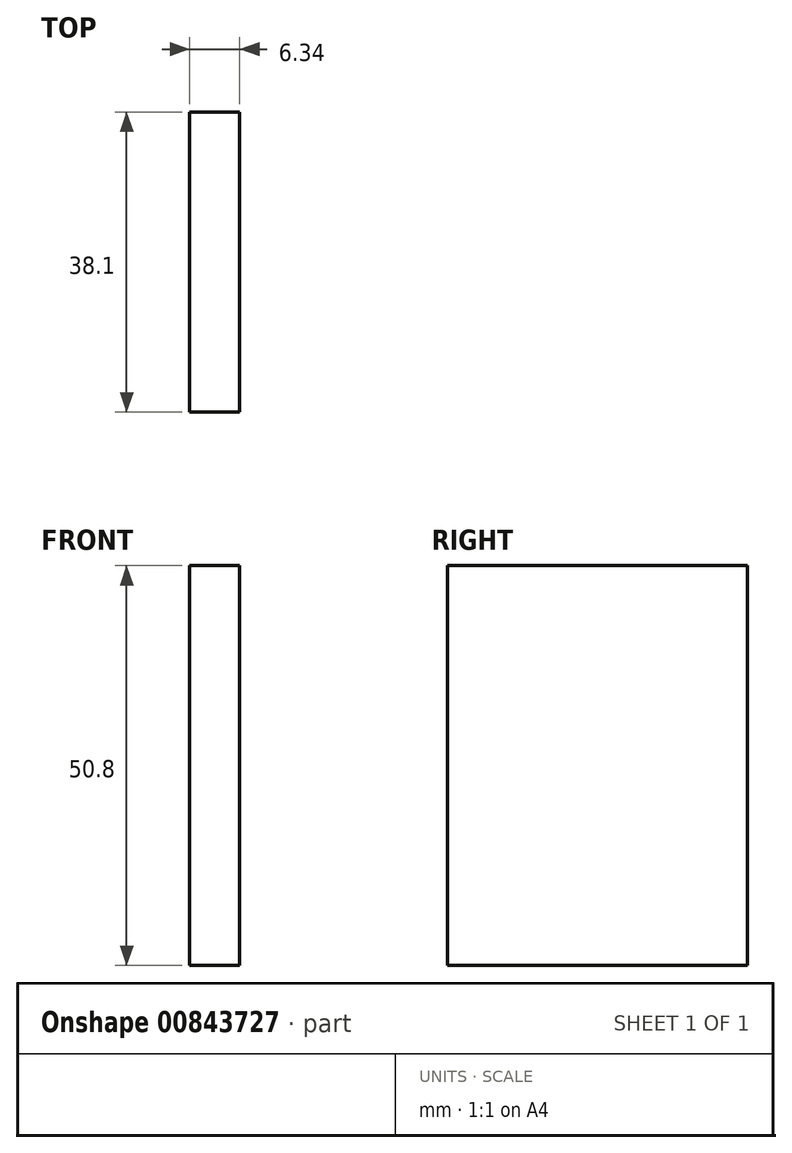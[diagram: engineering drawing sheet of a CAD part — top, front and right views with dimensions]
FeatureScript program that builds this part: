
annotation { "Feature Type Name" : "Feature", "Feature Type Description" : "" }
export const myFeature = defineFeature(function(context is Context, id is Id, definition is map)
    precondition{}
    {
        {
            var Q0;
            Q0=qCreatedBy(makeId("Front.planeOp"),FACE);
            var sketch = newSketch(context, id + "F0", { "sketchPlane" : qUnion([Q0])});
            skLineSegment(sketch, "E0.bottom", {"start": v(3.17, 25.4) * mm, "end": v(-3.18, 25.4) * mm});
            skLineSegment(sketch, "E0.top", {"start": v(3.17, -25.4) * mm, "end": v(-3.17, -25.4) * mm});
            skLineSegment(sketch, "E0.left", {"start": v(3.17, 25.4) * mm, "end": v(3.17, -25.4) * mm});
            skLineSegment(sketch, "E0.right", {"start": v(-3.18, 25.4) * mm, "end": v(-3.17, -25.4) * mm});
            skPoint(sketch, "E0.middle", {"position": v(0, 0) * mm});
            skSolve(sketch);
        }
        {
            var Q0;
            Q0=qSketchRegion(id+"F0",true);
            extrude(context, id + "F1", {"entities" : qUnion([Q0]), "depth" : 38.1 * mm, "offsetDistance" : 25.4 * mm});
        }
    });
